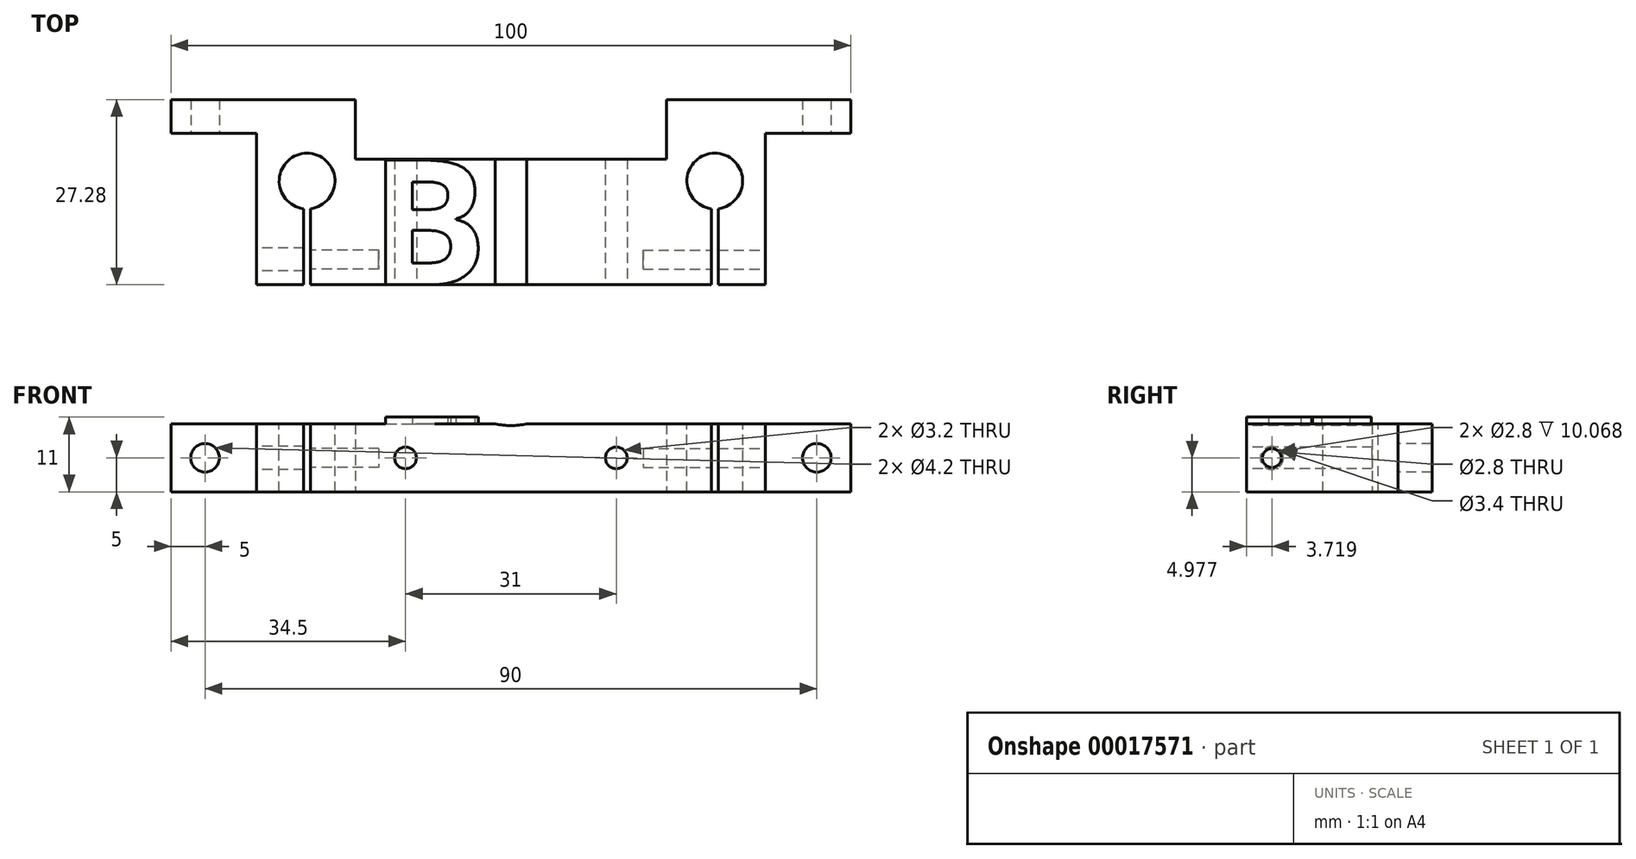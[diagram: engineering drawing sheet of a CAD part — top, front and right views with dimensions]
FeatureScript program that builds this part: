
annotation { "Feature Type Name" : "Feature", "Feature Type Description" : "" }
export const myFeature = defineFeature(function(context is Context, id is Id, definition is map)
    precondition{}
    {
        {
            var Q0;
            Q0=qCreatedBy(makeId("Top.planeOp"),FACE);
            var sketch = newSketch(context, id + "F0", { "sketchPlane" : qUnion([Q0])});
            skLineSegment(sketch, "E0", {"start": v(0, -13.82) * mm, "end": v(-37.44, -13.82) * mm});
            skLineSegment(sketch, "E1", {"start": v(-37.44, -13.82) * mm, "end": v(-37.44, 8.46) * mm});
            skLineSegment(sketch, "E2", {"start": v(-37.44, 8.46) * mm, "end": v(-50, 8.46) * mm});
            skLineSegment(sketch, "E3", {"start": v(-50, 8.46) * mm, "end": v(-50, 13.46) * mm});
            skLineSegment(sketch, "E4", {"start": v(-50, 13.46) * mm, "end": v(-22.87, 13.46) * mm});
            skLineSegment(sketch, "E5", {"start": v(-22.87, 13.46) * mm, "end": v(-22.87, 4.68) * mm});
            skLineSegment(sketch, "E6", {"start": v(-22.87, 4.68) * mm, "end": v(0, 4.68) * mm});
            skLineSegment(sketch, "E7", {"start": v(0, 4.68) * mm, "end": v(0, -13.82) * mm});
            skSolve(sketch);
        }
        {
            var Q0;
            Q0=qSketchRegion(id+"F0",true);
            extrude(context, id + "F1", {"entities" : qUnion([Q0]), "depth" : 10 * mm});
        }
        {
            var Q0;
            Q0=makeQuery(id+"F1.opExtrude","SWEPT_FACE",FACE,{"disambiguationData":[OSD([sQuery(id+"F0.wireOp",EDGE,"E0")])]});
            var sketch = newSketch(context, id + "F2", { "sketchPlane" : qUnion([Q0])});
            skLineSegment(sketch, "E8", {"start": v(0, 5) * mm, "end": v(0, 5) * mm});
            skCircle(sketch, "E9", {"center": v(-15.5, 5) * mm, "radius": 1.6 * mm});
            skCircle(sketch, "E10", {"center": v(0, 20.5) * mm, "radius": 10.75 * mm});
            skSolve(sketch);
        }
        {
            var Q0;
            Q0=qSketchRegion(id+"F2",true);
            extrude(context, id + "F3", {"entities" : qUnion([Q0]), "operationType" : NewBodyOperationType.REMOVE, "endBound" : BoundingType.THROUGH_ALL, "oppositeDirection" : true, "depth" : 25 * mm});
        }
        {
            var Q0;
            Q0=makeQuery(id+"F1.opExtrude","SWEPT_FACE",FACE,{"disambiguationData":[OSD([sQuery(id+"F0.wireOp",EDGE,"E2")])]});
            var sketch = newSketch(context, id + "F4", { "sketchPlane" : qUnion([Q0])});
            skLineSegment(sketch, "E11", {"start": v(-50, 5) * mm, "end": v(-37.44, 5) * mm, "construction": true});
            skLineSegment(sketch, "E12", {"start": v(-43.72, 10) * mm, "end": v(-43.72, 0) * mm, "construction": true});
            skCircle(sketch, "E13", {"center": v(-45, 5) * mm, "radius": 2.1 * mm});
            skSolve(sketch);
        }
        {
            var Q0;
            Q0=qSketchRegion(id+"F4",true);
            extrude(context, id + "F5", {"entities" : qUnion([Q0]), "operationType" : NewBodyOperationType.REMOVE, "endBound" : BoundingType.THROUGH_ALL, "oppositeDirection" : true, "depth" : 25 * mm});
        }
        {
            var Q0;
            {var subQ0=makeQuery(id+"F1.opExtrude","CAP_FACE",FACE,{"disambiguationData":[OSD([sQuery(id+"F0.wireOp",EDGE,"E0"),sQuery(id+"F0.wireOp",EDGE,"fd64a43a-5635-4f94-a977-4dd36923accb"),sQuery(id+"F0.wireOp",EDGE,"1334f7d4-4c90-4769-8fa3-fe5f576fb005"),sQuery(id+"F0.wireOp",EDGE,"E1"),sQuery(id+"F0.wireOp",EDGE,"E2"),sQuery(id+"F0.wireOp",EDGE,"E3"),sQuery(id+"F0.wireOp",EDGE,"E4"),sQuery(id+"F0.wireOp",EDGE,"E5"),sQuery(id+"F0.wireOp",EDGE,"E6"),sQuery(id+"F0.wireOp",EDGE,"E7")])],"isStart":false});Q0=makeQuery(id+"F10.boolean.opBoolean","MERGE",FACE,{"derivedFrom":[subQ0,makeQuery(id+"F10.opPattern","COPY",FACE,{"derivedFrom":subQ0,"instanceName":"1"})]});}
            var sketch = newSketch(context, id + "F6", { "sketchPlane" : qUnion([Q0])});
            skCircle(sketch, "E14", {"center": v(-30, 1.46) * mm, "radius": 4.1 * mm});
            skLineSegment(sketch, "E15", {"start": v(-30, 1.46) * mm, "end": v(-30, -13.82) * mm, "construction": true});
            skLineSegment(sketch, "E16.bottom", {"start": v(-30.49, -2.04) * mm, "end": v(-29.51, -2.04) * mm});
            skLineSegment(sketch, "E16.top", {"start": v(-30.49, -14.16) * mm, "end": v(-29.51, -14.16) * mm});
            skLineSegment(sketch, "E16.left", {"start": v(-30.49, -2.04) * mm, "end": v(-30.49, -14.16) * mm});
            skLineSegment(sketch, "E16.right", {"start": v(-29.51, -2.04) * mm, "end": v(-29.51, -14.16) * mm});
            skPoint(sketch, "E17", {"position": v(-30, -2.04) * mm});
            skSolve(sketch);
        }
        {
            var Q0;
            Q0=qSketchRegion(id+"F6",true);
            var Q1;
            {var subQ3=sQuery(id+"F6.wireOp",EDGE,"E16.bottom");Q1=makeQuery(id+"F6.imprint","IMPRINT",FACE,{"disambiguationData":[TD([[makeQuery(id+"F6.imprint","IMPRINT",EDGE,{"derivedFrom":subQ3}),-1.0]])]});}
            extrude(context, id + "F7", {"entities" : qUnion([Q0, Q1]), "operationType" : NewBodyOperationType.REMOVE, "endBound" : BoundingType.THROUGH_ALL, "oppositeDirection" : true, "depth" : 25 * mm});
        }
        {
            var Q0;
            Q0=makeQuery(id+"F1.opExtrude","SWEPT_FACE",FACE,{"disambiguationData":[OSD([sQuery(id+"F0.wireOp",EDGE,"E1")])]});
            var sketch = newSketch(context, id + "F8", { "sketchPlane" : qUnion([Q0])});
            skCircle(sketch, "E18", {"center": v(10.1, 4.98) * mm, "radius": 1.4 * mm});
            skCircle(sketch, "E19", {"center": v(10.1, 4.98) * mm, "radius": 1.7 * mm});
            skSolve(sketch);
        }
        {
            var Q0;
            Q0=makeQuery(id+"F8.imprint","IMPRINT",FACE,{"disambiguationData":[TD([[makeQuery(id+"F8.imprint","IMPRINT",EDGE,{"derivedFrom":sQuery(id+"F8.wireOp",EDGE,"E18")}),1.0]])]});
            extrude(context, id + "F9", {"entities" : qUnion([Q0]), "operationType" : NewBodyOperationType.REMOVE, "oppositeDirection" : true, "depth" : 18 * mm});
        }
        {
            var Q0;
            Q0=makeQuery(id+"F1.opExtrude","SWEPT_BODY",BODY,{"disambiguationData":[OSD([sQuery(id+"F0.wireOp",EDGE,"E0"),sQuery(id+"F0.wireOp",EDGE,"fd64a43a-5635-4f94-a977-4dd36923accb"),sQuery(id+"F0.wireOp",EDGE,"1334f7d4-4c90-4769-8fa3-fe5f576fb005"),sQuery(id+"F0.wireOp",EDGE,"E1"),sQuery(id+"F0.wireOp",EDGE,"E2"),sQuery(id+"F0.wireOp",EDGE,"E3"),sQuery(id+"F0.wireOp",EDGE,"E4"),sQuery(id+"F0.wireOp",EDGE,"E5"),sQuery(id+"F0.wireOp",EDGE,"E6"),sQuery(id+"F0.wireOp",EDGE,"E7")])]});
            var Q1;
            Q1=qCreatedBy(makeId("Right.planeOp"),FACE);
            mirror(context, id + "F10", {"operationType" : NewBodyOperationType.ADD, "entities" : qUnion([Q0]), "mirrorPlane" : qUnion([Q1])});
        }
        {
            var Q0;
            Q0=makeQuery(id+"F1.opExtrude","CAP_FACE",FACE,{"disambiguationData":[OSD([sQuery(id+"F0.wireOp",EDGE,"E0"),sQuery(id+"F0.wireOp",EDGE,"E1"),sQuery(id+"F0.wireOp",EDGE,"E2"),sQuery(id+"F0.wireOp",EDGE,"E3"),sQuery(id+"F0.wireOp",EDGE,"E4"),sQuery(id+"F0.wireOp",EDGE,"E5"),sQuery(id+"F0.wireOp",EDGE,"E6"),sQuery(id+"F0.wireOp",EDGE,"E7")])],"isStart":false});
            var sketch = newSketch(context, id + "F11", { "sketchPlane" : qUnion([Q0])});
            skText(sketch, "E20", { "text": "B", "fontName": "OpenSans-Bold.ttf"});
            const initialGuessF11  = {"E20": [-0.02073, -0.01382, 1, 0, 0.0185]};
            skSetInitialGuess(sketch, initialGuessF11);
            skSolve(sketch);
        }
        {
            var Q0;
            Q0=qSketchRegion(id+"F11",true);
            extrude(context, id + "F12", {"entities" : qUnion([Q0]), "operationType" : NewBodyOperationType.ADD, "depth" : 1 * mm});
        }
        {
            var Q0;
            Q0=makeQuery(id+"F8.imprint","IMPRINT",FACE,{"disambiguationData":[TD([[makeQuery(id+"F8.imprint","IMPRINT",EDGE,{"derivedFrom":sQuery(id+"F8.wireOp",EDGE,"E18")}),1.0]])]});
            var Q1;
            Q1=makeQuery(id+"F8.imprint","IMPRINT",FACE,{"disambiguationData":[TD([[makeQuery(id+"F8.imprint","IMPRINT",EDGE,{"derivedFrom":sQuery(id+"F8.wireOp",EDGE,"E18")}),-1.0]])]});
            extrude(context, id + "F13", {"entities" : qUnion([Q0, Q1]), "operationType" : NewBodyOperationType.REMOVE, "endBound" : BoundingType.UP_TO_NEXT, "oppositeDirection" : true, "depth" : 25 * mm});
        }
    });
